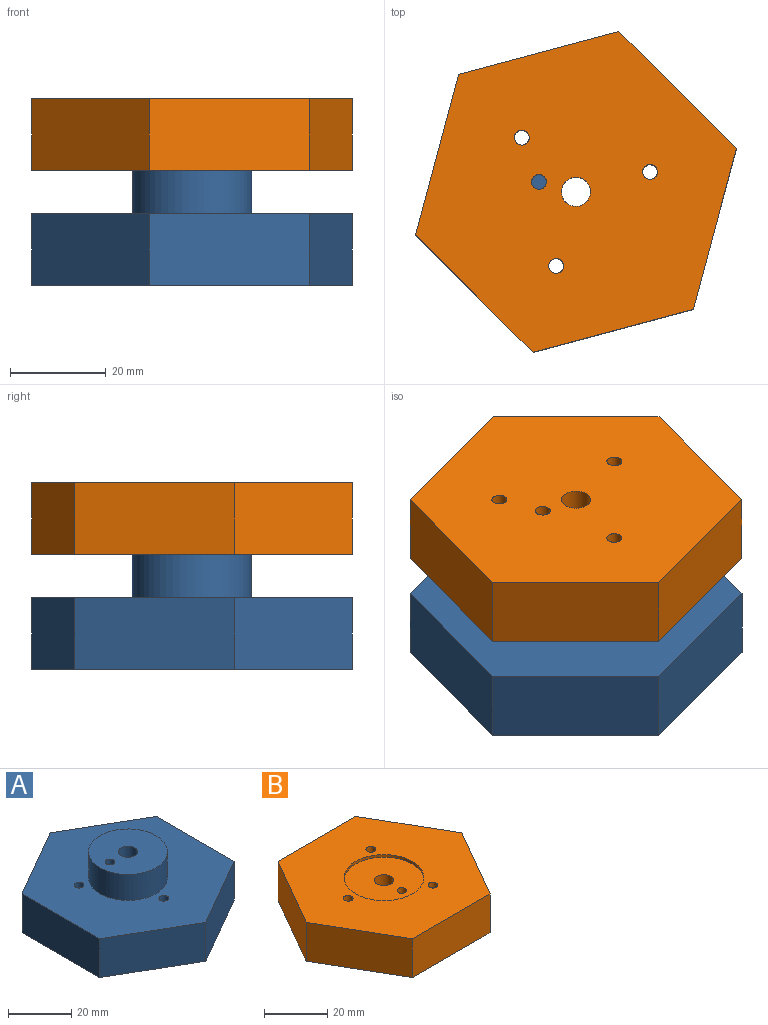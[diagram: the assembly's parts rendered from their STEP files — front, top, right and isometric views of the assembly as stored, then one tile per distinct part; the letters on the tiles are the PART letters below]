
ASSEMBLY  parts=2 mates=1
PART A: 24 faces, bbox 60x69.3x25 mm
  f0: cylinder r=1.55mm len=9mm, axis (0,0,-1), area 87.7mm2, adj f14,f16
  f1: cylinder r=1.55mm len=9mm, axis (0,0,-1), area 87.7mm2, adj f14,f18
  f2: cylinder r=1.55mm len=9mm, axis (0,0,-1), area 87.7mm2, adj f14,f20
  f3: plane 30x17.32mm, normal (-0.5,0.87,0), area 519.6mm2, adj f4,f8,f11,f14
  f4: plane 34.64x15mm, normal (-1,0,0), area 519.6mm2, adj f3,f5,f11,f14
  f5: plane 30x17.32mm, normal (-0.5,-0.87,0), area 519.6mm2, adj f4,f6,f11,f14
  f6: plane 30x17.32mm, normal (0.5,-0.87,0), area 519.6mm2, adj f5,f7,f11,f14
  f7: plane 34.64x15mm, normal (1,0,0), area 519.6mm2, adj f6,f8,f11,f14
  f8: plane 30x17.32mm, normal (0.5,0.87,0), area 519.6mm2, adj f3,f7,f11,f14
  f9: plane 24.9x24.9mm, normal (0,0,1), area 450.2mm2, adj f10,f15,f22
  f10: cylinder r=3.05mm len=17.5mm, axis (0,0,-1), area 335.4mm2, adj f9,f12
  f11: plane 69.28x60mm, normal (0,0,-1), area 2819mm2, adj f3,f4,f5,f6,f7,f8,f13,f17
  f12: plane 16.5x16.5mm, normal (0,0,-1), area 184.6mm2, adj f10,f13
  f13: cylinder r=8.25mm len=16.5mm, axis (0,0,-1), area 388.8mm2, adj f11,f12
  f14: plane 69.28x60mm, normal (0,0,1), area 2608.1mm2, adj f0,f1,f2,f3,f4,f5,f6,f7
  f15: cylinder r=12.45mm len=24.9mm, axis (0,0,1), area 782.3mm2, adj f9,f14
  f16: plane 6x6mm, normal (0,0,-1), area 20.7mm2, adj f0,f17
  f17: cylinder r=3mm len=6mm, axis (0,0,-1), area 113.1mm2, adj f11,f16
  f18: plane 6x6mm, normal (0,0,-1), area 20.7mm2, adj f1,f19
  f19: cylinder r=3mm len=6mm, axis (0,0,-1), area 113.1mm2, adj f11,f18
  f20: plane 6x6mm, normal (0,0,-1), area 20.7mm2, adj f2,f21
  f21: cylinder r=3mm len=6mm, axis (0,0,-1), area 113.1mm2, adj f11,f20
  f22: cylinder r=1.55mm len=15mm, axis (0,0,1), area 146.1mm2, adj f9,f23
  f23: plane 3.1x3.1mm, normal (0,0,1), area 7.5mm2, adj f22
PART B: 15 faces, bbox 69.3x60x15 mm
  f0: plane 30x17.32mm, normal (0.87,0.5,0), area 519.6mm2, adj f1,f5,f6,f7
  f1: plane 34.64x15mm, normal (0,1,0), area 519.6mm2, adj f0,f2,f6,f7
  f2: plane 30x17.32mm, normal (-0.87,0.5,0), area 519.6mm2, adj f1,f3,f6,f7
  f3: plane 30x17.32mm, normal (-0.87,-0.5,0), area 519.6mm2, adj f2,f4,f6,f7
  f4: plane 34.64x15mm, normal (0,-1,0), area 519.6mm2, adj f3,f5,f6,f7
  f5: plane 30x17.32mm, normal (0.87,-0.5,0), area 519.6mm2, adj f0,f4,f6,f7
  f6: plane 69.28x60mm, normal (0,0,1), area 2596.3mm2, adj f0,f1,f2,f3,f4,f5,f8,f12
  f7: plane 69.28x60mm, normal (0,0,-1), area 3058.3mm2, adj f0,f1,f2,f3,f4,f5,f10,f11
  f8: cylinder r=12.6mm len=25.2mm, axis (0,0,1), area 79.2mm2, adj f6,f9
  f9: plane 25.2x25.2mm, normal (0,0,1), area 462mm2, adj f8,f10,f11
  f10: cylinder r=1.55mm len=14mm, axis (0,0,-1), area 136.3mm2, adj f7,f9
  f11: cylinder r=3.05mm len=14mm, axis (0,0,-1), area 268.3mm2, adj f7,f9
  f12: cylinder r=1.55mm len=15mm, axis (0,0,-1), area 146.1mm2, adj f6,f7
  f13: cylinder r=1.55mm len=15mm, axis (0,0,-1), area 146.1mm2, adj f6,f7
  f14: cylinder r=1.55mm len=15mm, axis (0,0,-1), area 146.1mm2, adj f6,f7
PLACE A rot(axis=(0,0,-1),15deg) t=(-4.97,13.1,0)mm
PLACE B rot(axis=(0.79,0.61,0),180deg) t=(-4.97,13.1,39)mm
MATE slider B.f8 <-> A.f10  axis (0,0,-1) through (-4.97,13.1,25)mm
